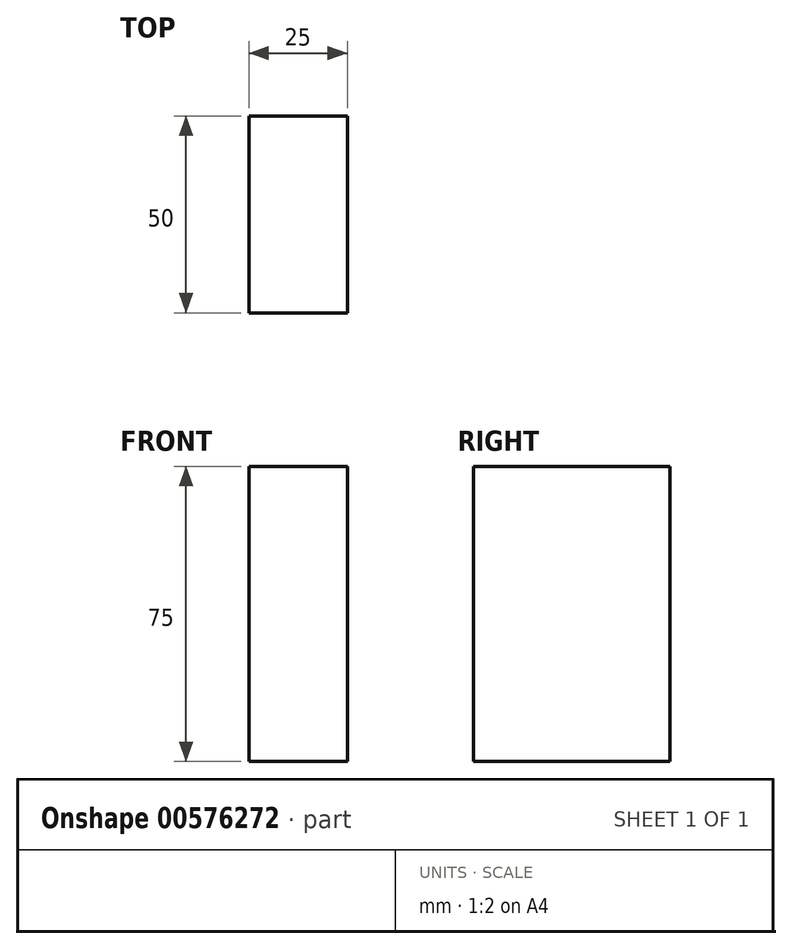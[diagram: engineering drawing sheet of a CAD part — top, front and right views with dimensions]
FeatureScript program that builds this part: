
annotation { "Feature Type Name" : "Feature", "Feature Type Description" : "" }
export const myFeature = defineFeature(function(context is Context, id is Id, definition is map)
    precondition{}
    {
        {
            var Q0;
            Q0=qCreatedBy(makeId("Top.planeOp"),FACE);
            var sketch = newSketch(context, id + "F0", { "sketchPlane" : qUnion([Q0])});
            skLineSegment(sketch, "E0.bottom", {"start": v(-32.33, 46.36) * mm, "end": v(-7.33, 46.36) * mm});
            skLineSegment(sketch, "E0.top", {"start": v(-32.33, -3.64) * mm, "end": v(-7.33, -3.64) * mm});
            skLineSegment(sketch, "E0.left", {"start": v(-32.33, 46.36) * mm, "end": v(-32.33, -3.64) * mm});
            skLineSegment(sketch, "E0.right", {"start": v(-7.33, 46.36) * mm, "end": v(-7.33, -3.64) * mm});
            skSolve(sketch);
        }
        {
            var Q0;
            Q0 = qSketchRegion(id + "F0", true);
            extrude(context, id + "F1", {"entities" : qUnion([Q0]), "depth" : 75 * mm, "offsetDistance" : 25 * mm});
        }
    });
